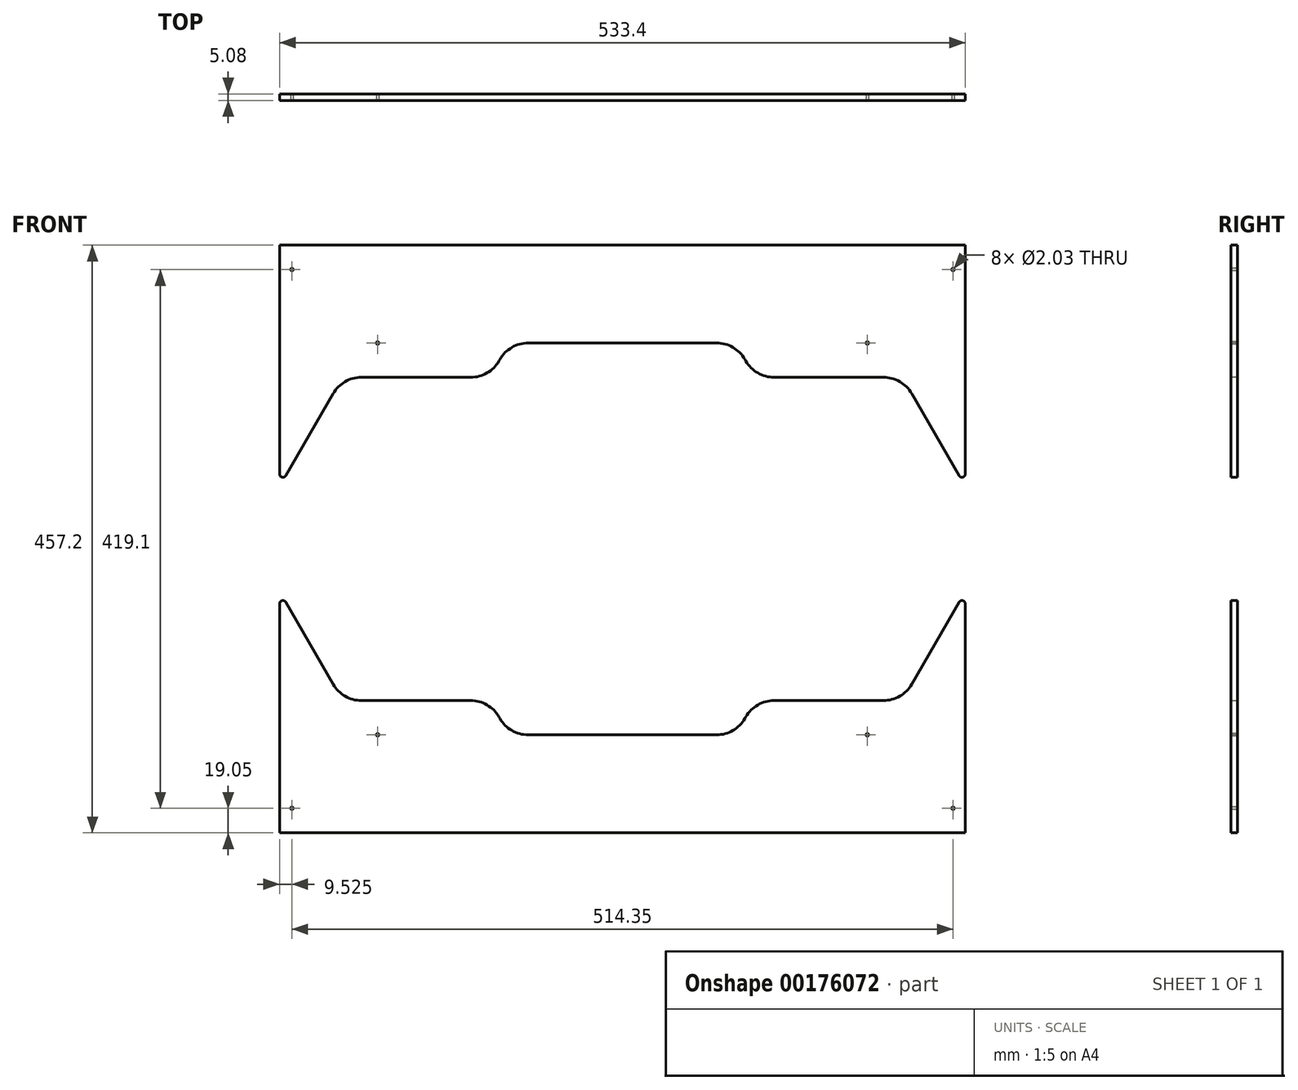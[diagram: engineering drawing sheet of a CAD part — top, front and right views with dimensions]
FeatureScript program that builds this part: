
annotation { "Feature Type Name" : "Feature", "Feature Type Description" : "" }
export const myFeature = defineFeature(function(context is Context, id is Id, definition is map)
    precondition{}
    {
        {
            var Q0;
            Q0=qCreatedBy(makeId("Front.planeOp"),FACE);
            var sketch = newSketch(context, id + "F0", { "sketchPlane" : qUnion([Q0])});
            skLineSegment(sketch, "E0.bottom", {"start": v(0, 0) * mm, "end": v(533.4, 0) * mm});
            skLineSegment(sketch, "E0.top", {"start": v(0, 457.2) * mm, "end": v(533.4, 457.2) * mm});
            skLineSegment(sketch, "E0.left", {"start": v(0, 0) * mm, "end": v(0, 457.2) * mm});
            skLineSegment(sketch, "E0.right", {"start": v(533.4, 0) * mm, "end": v(533.4, 457.2) * mm});
            skCircle(sketch, "E1.cCircle", {"center": v(121.52, 228.6) * mm, "radius": 125.73 * mm, "construction": true});
            skLineSegment(sketch, "E1.0", {"start": v(194.1, 354.33) * mm, "end": v(266.7, 228.6) * mm, "construction": true});
            skLineSegment(sketch, "E1.1", {"start": v(266.7, 228.6) * mm, "end": v(194.1, 102.87) * mm, "construction": true});
            skLineSegment(sketch, "E1.2", {"start": v(194.1, 102.87) * mm, "end": v(63.6, 102.87) * mm});
            skLineSegment(sketch, "E1.3", {"start": v(41.6, 115.57) * mm, "end": v(-16.33, 215.9) * mm});
            skLineSegment(sketch, "E1.4", {"start": v(-16.33, 241.3) * mm, "end": v(41.6, 341.63) * mm});
            skLineSegment(sketch, "E1.5", {"start": v(63.6, 354.33) * mm, "end": v(194.1, 354.33) * mm});
            skPoint(sketch, "E1.0.midPoint", {"position": v(230.4, 291.46) * mm});
            skCircle(sketch, "E2.cCircle", {"center": v(411.88, 228.6) * mm, "radius": 125.73 * mm, "construction": true});
            skLineSegment(sketch, "E2.0", {"start": v(491.8, 341.63) * mm, "end": v(549.73, 241.3) * mm});
            skLineSegment(sketch, "E2.1", {"start": v(549.73, 215.9) * mm, "end": v(491.8, 115.57) * mm});
            skLineSegment(sketch, "E2.2", {"start": v(469.8, 102.87) * mm, "end": v(339.3, 102.87) * mm});
            skLineSegment(sketch, "E2.3", {"start": v(339.3, 102.87) * mm, "end": v(266.7, 228.6) * mm, "construction": true});
            skLineSegment(sketch, "E2.4", {"start": v(266.7, 228.6) * mm, "end": v(339.3, 354.33) * mm, "construction": true});
            skLineSegment(sketch, "E2.5", {"start": v(339.3, 354.33) * mm, "end": v(469.8, 354.33) * mm});
            skPoint(sketch, "E2.0.midPoint", {"position": v(520.77, 291.46) * mm});
            skLineSegment(sketch, "E3", {"start": v(194.1, 354.33) * mm, "end": v(339.3, 354.33) * mm});
            skLineSegment(sketch, "E4", {"start": v(339.3, 102.87) * mm, "end": v(194.1, 102.87) * mm, "construction": true});
            skPoint(sketch, "E5.visualSharp", {"position": v(48.93, 354.33) * mm});
            skArc(sketch, "E5.filletArc", {"start": v(63.6, 354.33) * mm, "mid": v(50.9, 350.93) * mm, "end": v(41.6, 341.63) * mm});
            skPoint(sketch, "E6.visualSharp", {"position": v(-23.66, 228.6) * mm});
            skArc(sketch, "E6.filletArc", {"start": v(-16.33, 241.3) * mm, "mid": v(-19.73, 228.6) * mm, "end": v(-16.33, 215.9) * mm});
            skPoint(sketch, "E7.visualSharp", {"position": v(48.93, 102.87) * mm});
            skArc(sketch, "E7.filletArc", {"start": v(41.6, 115.57) * mm, "mid": v(50.9, 106.27) * mm, "end": v(63.6, 102.87) * mm});
            skPoint(sketch, "E8.visualSharp", {"position": v(484.47, 102.87) * mm});
            skArc(sketch, "E8.filletArc", {"start": v(469.8, 102.87) * mm, "mid": v(482.5, 106.27) * mm, "end": v(491.8, 115.57) * mm});
            skPoint(sketch, "E9.visualSharp", {"position": v(557.06, 228.6) * mm});
            skArc(sketch, "E9.filletArc", {"start": v(549.73, 215.9) * mm, "mid": v(553.13, 228.6) * mm, "end": v(549.73, 241.3) * mm});
            skPoint(sketch, "E10.visualSharp", {"position": v(484.47, 354.33) * mm});
            skArc(sketch, "E10.filletArc", {"start": v(491.8, 341.63) * mm, "mid": v(482.5, 350.93) * mm, "end": v(469.8, 354.33) * mm});
            skPoint(sketch, "E11", {"position": v(266.7, 457.2) * mm});
            skPoint(sketch, "E12", {"position": v(0, 228.6) * mm});
            skCircle(sketch, "E13.cCircle", {"center": v(266.7, 228.6) * mm, "radius": 125.73 * mm, "construction": true});
            skLineSegment(sketch, "E13.0", {"start": v(194.1, 354.33) * mm, "end": v(339.3, 354.33) * mm, "construction": true});
            skLineSegment(sketch, "E13.1", {"start": v(339.3, 354.33) * mm, "end": v(411.88, 228.6) * mm, "construction": true});
            skLineSegment(sketch, "E13.2", {"start": v(411.88, 228.6) * mm, "end": v(339.3, 102.87) * mm, "construction": true});
            skLineSegment(sketch, "E13.3", {"start": v(339.3, 102.87) * mm, "end": v(194.1, 102.87) * mm});
            skLineSegment(sketch, "E13.4", {"start": v(194.1, 102.87) * mm, "end": v(121.52, 228.6) * mm, "construction": true});
            skLineSegment(sketch, "E13.5", {"start": v(121.52, 228.6) * mm, "end": v(194.1, 354.33) * mm, "construction": true});
            skPoint(sketch, "E13.0.midPoint", {"position": v(266.7, 354.33) * mm});
            skLineSegment(sketch, "E14.bottom", {"start": v(196.06, 347.98) * mm, "end": v(221.46, 347.98) * mm});
            skLineSegment(sketch, "E14.top", {"start": v(196.06, 109.22) * mm, "end": v(221.46, 109.22) * mm});
            skLineSegment(sketch, "E14.left", {"start": v(196.06, 347.98) * mm, "end": v(196.06, 109.22) * mm});
            skLineSegment(sketch, "E14.right", {"start": v(221.46, 347.98) * mm, "end": v(221.46, 109.22) * mm});
            skLineSegment(sketch, "E15", {"start": v(208.76, 347.98) * mm, "end": v(208.76, 109.22) * mm, "construction": true});
            skPoint(sketch, "E16", {"position": v(208.76, 228.6) * mm});
            skLineSegment(sketch, "E17", {"start": v(266.7, 228.6) * mm, "end": v(266.7, 281.64) * mm, "construction": true});
            skLineSegment(sketch, "E18.MirrorCS", {"start": v(337.34, 109.22) * mm, "end": v(311.94, 109.22) * mm});
            skLineSegment(sketch, "E19.MirrorCS", {"start": v(311.94, 347.98) * mm, "end": v(311.94, 109.22) * mm});
            skLineSegment(sketch, "E20.MirrorCS", {"start": v(337.34, 347.98) * mm, "end": v(311.94, 347.98) * mm});
            skLineSegment(sketch, "E21.MirrorCS", {"start": v(337.34, 347.98) * mm, "end": v(337.34, 109.22) * mm});
            skSolve(sketch);
        }
        {
            var Q0;
            {var subQ1=sQuery(id+"F0.wireOp",EDGE,"E0.bottom");Q0=makeQuery(id+"F0.imprint","IMPRINT",FACE,{"disambiguationData":[TD([[makeQuery(id+"F0.imprint","IMPRINT",EDGE,{"derivedFrom":subQ1}),1.0]])]});}
            var Q1;
            {var subQ5=sQuery(id+"F0.wireOp",EDGE,"E0.top");Q1=makeQuery(id+"F0.imprint","IMPRINT",FACE,{"disambiguationData":[TD([[makeQuery(id+"F0.imprint","IMPRINT",EDGE,{"derivedFrom":subQ5}),-1.0]])]});}
            extrude(context, id + "F1", {"entities" : qUnion([Q0, Q1]), "depth" : 5.08 * mm});
        }
        {
            var Q0;
            Q0=makeQuery(id+"F1.opExtrude","CAP_FACE",FACE,{"disambiguationData":[OSD([sQuery(id+"F0.wireOp",EDGE,"E0.bottom"),sQuery(id+"F0.wireOp",EDGE,"E0.top"),sQuery(id+"F0.wireOp",EDGE,"E0.left"),sQuery(id+"F0.wireOp",EDGE,"E0.right"),sQuery(id+"F0.wireOp",EDGE,"E14.bottom"),sQuery(id+"F0.wireOp",EDGE,"E14.top"),sQuery(id+"F0.wireOp",EDGE,"E14.left"),sQuery(id+"F0.wireOp",EDGE,"E14.right"),sQuery(id+"F0.wireOp",EDGE,"E18.MirrorCS"),sQuery(id+"F0.wireOp",EDGE,"E19.MirrorCS"),sQuery(id+"F0.wireOp",EDGE,"E20.MirrorCS"),sQuery(id+"F0.wireOp",EDGE,"E21.MirrorCS")])],"isStart":false});
            var sketch = newSketch(context, id + "F2", { "sketchPlane" : qUnion([Q0])});
            skCircle(sketch, "E22", {"center": v(9.53, 438.15) * mm, "radius": 1.02 * mm});
            skCircle(sketch, "E23.0.1.0", {"center": v(9.53, 19.05) * mm, "radius": 1.02 * mm});
            skCircle(sketch, "E23.1.0.0", {"center": v(523.88, 438.15) * mm, "radius": 1.02 * mm});
            skCircle(sketch, "E23.1.1.0", {"center": v(523.88, 19.05) * mm, "radius": 1.02 * mm});
            skLineSegment(sketch, "E23.direction2", {"start": v(9.53, 438.15) * mm, "end": v(9.53, 19.05) * mm, "construction": true});
            skSolve(sketch);
        }
        {
            var Q0;
            Q0=makeQuery(id+"F2.imprint","IMPRINT",FACE,{"disambiguationData":[TD([[makeQuery(id+"F2.imprint","IMPRINT",EDGE,{"derivedFrom":sQuery(id+"F2.wireOp",EDGE,"E22")}),1.0]])]});
            var Q1;
            Q1=makeQuery(id+"F2.imprint","IMPRINT",FACE,{"disambiguationData":[TD([[makeQuery(id+"F2.imprint","IMPRINT",EDGE,{"derivedFrom":sQuery(id+"F2.wireOp",EDGE,"E23.1.0.0")}),1.0]])]});
            var Q2;
            Q2=makeQuery(id+"F2.imprint","IMPRINT",FACE,{"disambiguationData":[TD([[makeQuery(id+"F2.imprint","IMPRINT",EDGE,{"derivedFrom":sQuery(id+"F2.wireOp",EDGE,"E23.1.1.0")}),1.0]])]});
            var Q3;
            Q3=makeQuery(id+"F2.imprint","IMPRINT",FACE,{"disambiguationData":[TD([[makeQuery(id+"F2.imprint","IMPRINT",EDGE,{"derivedFrom":sQuery(id+"F2.wireOp",EDGE,"E23.0.1.0")}),1.0]])]});
            extrude(context, id + "F3", {"entities" : qUnion([Q0, Q1, Q2, Q3]), "operationType" : NewBodyOperationType.REMOVE, "endBound" : BoundingType.THROUGH_ALL, "oppositeDirection" : true, "depth" : 25.4 * mm});
        }
        {
            var Q0;
            Q0=makeQuery(id+"F1.opExtrude","CAP_FACE",FACE,{"disambiguationData":[OSD([sQuery(id+"F0.wireOp",EDGE,"E0.bottom"),sQuery(id+"F0.wireOp",EDGE,"E0.left"),sQuery(id+"F0.wireOp",EDGE,"E0.right"),sQuery(id+"F0.wireOp",EDGE,"E1.2"),sQuery(id+"F0.wireOp",EDGE,"E1.3"),sQuery(id+"F0.wireOp",EDGE,"E2.1"),sQuery(id+"F0.wireOp",EDGE,"E2.2"),sQuery(id+"F0.wireOp",EDGE,"E7.filletArc"),sQuery(id+"F0.wireOp",EDGE,"E8.filletArc"),sQuery(id+"F0.wireOp",EDGE,"E13.3")])],"isStart":false});
            var sketch = newSketch(context, id + "F4", { "sketchPlane" : qUnion([Q0])});
            skCircle(sketch, "E24", {"center": v(76.2, 381) * mm, "radius": 1.02 * mm});
            skCircle(sketch, "E25.0.1.0", {"center": v(76.2, 76.2) * mm, "radius": 1.02 * mm});
            skCircle(sketch, "E25.1.0.0", {"center": v(457.2, 381) * mm, "radius": 1.02 * mm});
            skCircle(sketch, "E25.1.1.0", {"center": v(457.2, 76.2) * mm, "radius": 1.02 * mm});
            skSolve(sketch);
        }
        {
            var Q0;
            Q0=makeQuery(id+"F4.imprint","IMPRINT",FACE,{"disambiguationData":[TD([[makeQuery(id+"F4.imprint","IMPRINT",EDGE,{"derivedFrom":sQuery(id+"F4.wireOp",EDGE,"E24")}),1.0]])]});
            var Q1;
            Q1=makeQuery(id+"F4.imprint","IMPRINT",FACE,{"disambiguationData":[TD([[makeQuery(id+"F4.imprint","IMPRINT",EDGE,{"derivedFrom":sQuery(id+"F4.wireOp",EDGE,"E25.1.1.0")}),1.0]])]});
            var Q2;
            Q2=makeQuery(id+"F4.imprint","IMPRINT",FACE,{"disambiguationData":[TD([[makeQuery(id+"F4.imprint","IMPRINT",EDGE,{"derivedFrom":sQuery(id+"F4.wireOp",EDGE,"E25.1.0.0")}),1.0]])]});
            var Q3;
            Q3=makeQuery(id+"F4.imprint","IMPRINT",FACE,{"disambiguationData":[TD([[makeQuery(id+"F4.imprint","IMPRINT",EDGE,{"derivedFrom":sQuery(id+"F4.wireOp",EDGE,"E25.0.1.0")}),1.0]])]});
            extrude(context, id + "F5", {"entities" : qUnion([Q0, Q1, Q2, Q3]), "operationType" : NewBodyOperationType.REMOVE, "endBound" : BoundingType.THROUGH_ALL, "oppositeDirection" : true, "depth" : 25.4 * mm});
        }
        {
            var Q0;
            Q0=makeQuery(id+"F1.opExtrude","CAP_FACE",FACE,{"disambiguationData":[OSD([sQuery(id+"F0.wireOp",EDGE,"E0.top"),sQuery(id+"F0.wireOp",EDGE,"E0.left"),sQuery(id+"F0.wireOp",EDGE,"E0.right"),sQuery(id+"F0.wireOp",EDGE,"E1.4"),sQuery(id+"F0.wireOp",EDGE,"E1.5"),sQuery(id+"F0.wireOp",EDGE,"E2.0"),sQuery(id+"F0.wireOp",EDGE,"E2.5"),sQuery(id+"F0.wireOp",EDGE,"E3"),sQuery(id+"F0.wireOp",EDGE,"E5.filletArc"),sQuery(id+"F0.wireOp",EDGE,"E10.filletArc")])],"isStart":false});
            var sketch = newSketch(context, id + "F6", { "sketchPlane" : qUnion([Q0])});
            skCircle(sketch, "E26.cCircle", {"center": v(266.7, 228.6) * mm, "radius": 127 * mm, "construction": true});
            skLineSegment(sketch, "E26.0", {"start": v(340.02, 355.6) * mm, "end": v(413.35, 228.6) * mm});
            skLineSegment(sketch, "E26.1", {"start": v(413.35, 228.6) * mm, "end": v(340.02, 101.6) * mm});
            skLineSegment(sketch, "E26.2", {"start": v(340.02, 101.6) * mm, "end": v(193.38, 101.6) * mm});
            skLineSegment(sketch, "E26.3", {"start": v(193.38, 101.6) * mm, "end": v(120.05, 228.6) * mm});
            skLineSegment(sketch, "E26.4", {"start": v(120.05, 228.6) * mm, "end": v(193.38, 355.6) * mm});
            skLineSegment(sketch, "E26.5", {"start": v(193.38, 355.6) * mm, "end": v(340.02, 355.6) * mm});
            skPoint(sketch, "E26.0.midPoint", {"position": v(376.69, 292.1) * mm});
            skCircle(sketch, "E27.cCircle", {"center": v(266.7, 228.6) * mm, "radius": 152.4 * mm, "construction": true});
            skLineSegment(sketch, "E27.0", {"start": v(193.38, 381) * mm, "end": v(340.02, 381) * mm});
            skLineSegment(sketch, "E27.1", {"start": v(362.02, 368.3) * mm, "end": v(442.68, 228.6) * mm});
            skLineSegment(sketch, "E27.2", {"start": v(442.68, 228.6) * mm, "end": v(362.02, 88.9) * mm});
            skLineSegment(sketch, "E27.3", {"start": v(340.02, 76.2) * mm, "end": v(193.38, 76.2) * mm});
            skLineSegment(sketch, "E27.4", {"start": v(171.38, 88.9) * mm, "end": v(90.72, 228.6) * mm});
            skLineSegment(sketch, "E27.5", {"start": v(90.72, 228.6) * mm, "end": v(171.38, 368.3) * mm});
            skPoint(sketch, "E27.0.midPoint", {"position": v(266.7, 381) * mm});
            skPoint(sketch, "E28.visualSharp", {"position": v(178.71, 381) * mm});
            skArc(sketch, "E28.filletArc", {"start": v(193.38, 381) * mm, "mid": v(180.68, 377.6) * mm, "end": v(171.38, 368.3) * mm});
            skPoint(sketch, "E29.visualSharp", {"position": v(354.69, 381) * mm});
            skArc(sketch, "E29.filletArc", {"start": v(362.02, 368.3) * mm, "mid": v(352.72, 377.6) * mm, "end": v(340.02, 381) * mm});
            skPoint(sketch, "E30.visualSharp", {"position": v(354.69, 76.2) * mm});
            skArc(sketch, "E30.filletArc", {"start": v(340.02, 76.2) * mm, "mid": v(352.72, 79.6) * mm, "end": v(362.02, 88.9) * mm});
            skPoint(sketch, "E31.visualSharp", {"position": v(178.71, 76.2) * mm});
            skArc(sketch, "E31.filletArc", {"start": v(171.38, 88.9) * mm, "mid": v(180.68, 79.6) * mm, "end": v(193.38, 76.2) * mm});
            skSolve(sketch);
        }
        {
            var Q0;
            {var subQ1=sQuery(id+"F6.wireOp",EDGE,"E26.1");Q0=makeQuery(id+"F6.imprint","IMPRINT",FACE,{"disambiguationData":[TD([[makeQuery(id+"F6.imprint","IMPRINT",EDGE,{"derivedFrom":subQ1}),-1.0]])]});}
            var Q1;
            {var subQ0=sQuery(id+"F6.wireOp",EDGE,"E26.5");Q1=makeQuery(id+"F6.imprint","IMPRINT",FACE,{"disambiguationData":[TD([[makeQuery(id+"F6.imprint","IMPRINT",EDGE,{"derivedFrom":subQ0}),-1.0]])]});}
            var Q2;
            {var subQ0=sQuery(id+"F6.wireOp",EDGE,"E26.5");Q2=makeQuery(id+"F6.imprint","IMPRINT",FACE,{"disambiguationData":[TD([[makeQuery(id+"F6.imprint","IMPRINT",EDGE,{"derivedFrom":subQ0}),1.0]])]});}
            var Q3;
            {var subQ12=sQuery(id+"F6.wireOp",EDGE,"E26.1");Q3=makeQuery(id+"F6.imprint","IMPRINT",FACE,{"disambiguationData":[TD([[makeQuery(id+"F6.imprint","IMPRINT",EDGE,{"derivedFrom":subQ12}),1.0]])]});}
            extrude(context, id + "F7", {"entities" : qUnion([Q0, Q1, Q2, Q3]), "operationType" : NewBodyOperationType.REMOVE, "endBound" : BoundingType.THROUGH_ALL, "oppositeDirection" : true, "depth" : 25.4 * mm});
        }
        {
            var Q0;
            Q0=makeQuery(id+"F7.boolean.opBoolean","INTERSECT",EDGE,{"derivedFrom":[makeQuery(id+"F1.opExtrude","SWEPT_FACE",FACE,{"disambiguationData":[OSD([sQuery(id+"F0.wireOp",EDGE,"E1.5"),sQuery(id+"F0.wireOp",EDGE,"E2.5"),sQuery(id+"F0.wireOp",EDGE,"E3")])]}),makeQuery(id+"F7.opExtrude","SWEPT_FACE",FACE,{"disambiguationData":[OSD([sQuery(id+"F6.wireOp",EDGE,"E27.5")])]})]});
            var Q1;
            Q1=makeQuery(id+"F7.boolean.opBoolean","INTERSECT",EDGE,{"derivedFrom":[makeQuery(id+"F1.opExtrude","SWEPT_FACE",FACE,{"disambiguationData":[OSD([sQuery(id+"F0.wireOp",EDGE,"E1.5"),sQuery(id+"F0.wireOp",EDGE,"E2.5"),sQuery(id+"F0.wireOp",EDGE,"E3")])]}),makeQuery(id+"F7.opExtrude","SWEPT_FACE",FACE,{"disambiguationData":[OSD([sQuery(id+"F6.wireOp",EDGE,"E27.1")])]})]});
            var Q2;
            Q2=makeQuery(id+"F7.boolean.opBoolean","INTERSECT",EDGE,{"derivedFrom":[makeQuery(id+"F1.opExtrude","SWEPT_FACE",FACE,{"disambiguationData":[OSD([sQuery(id+"F0.wireOp",EDGE,"E1.2"),sQuery(id+"F0.wireOp",EDGE,"E2.2"),sQuery(id+"F0.wireOp",EDGE,"E13.3")])]}),makeQuery(id+"F7.opExtrude","SWEPT_FACE",FACE,{"disambiguationData":[OSD([sQuery(id+"F6.wireOp",EDGE,"E27.4")])]})]});
            var Q3;
            Q3=makeQuery(id+"F7.boolean.opBoolean","INTERSECT",EDGE,{"derivedFrom":[makeQuery(id+"F1.opExtrude","SWEPT_FACE",FACE,{"disambiguationData":[OSD([sQuery(id+"F0.wireOp",EDGE,"E1.2"),sQuery(id+"F0.wireOp",EDGE,"E2.2"),sQuery(id+"F0.wireOp",EDGE,"E13.3")])]}),makeQuery(id+"F7.opExtrude","SWEPT_FACE",FACE,{"disambiguationData":[OSD([sQuery(id+"F6.wireOp",EDGE,"E27.2")])]})]});
            fillet(context, id + "F8", {"entities" : qUnion([Q0, Q1, Q2, Q3]), "radius" : 25.4 * mm, "tangentPropagation" : true, "allowEdgeOverflow" : false});
        }
        {
            var Q0;
            Q0=makeQuery(id+"F1.opExtrude","SWEPT_EDGE",EDGE,{"disambiguationData":[OSD([sQuery(id+"F0.wireOp",EDGE,"E0.left"),sQuery(id+"F0.wireOp",EDGE,"E1.4")])]});
            var Q1;
            Q1=makeQuery(id+"F1.opExtrude","SWEPT_EDGE",EDGE,{"disambiguationData":[OSD([sQuery(id+"F0.wireOp",EDGE,"E0.left"),sQuery(id+"F0.wireOp",EDGE,"E1.3")])]});
            var Q2;
            Q2=makeQuery(id+"F1.opExtrude","SWEPT_EDGE",EDGE,{"disambiguationData":[OSD([sQuery(id+"F0.wireOp",EDGE,"E0.right"),sQuery(id+"F0.wireOp",EDGE,"E2.0")])]});
            var Q3;
            Q3=makeQuery(id+"F1.opExtrude","SWEPT_EDGE",EDGE,{"disambiguationData":[OSD([sQuery(id+"F0.wireOp",EDGE,"E0.right"),sQuery(id+"F0.wireOp",EDGE,"E2.1")])]});
            fillet(context, id + "F9", {"entities" : qUnion([Q0, Q1, Q2, Q3]), "radius" : 2.54 * mm, "tangentPropagation" : true, "allowEdgeOverflow" : false});
        }
    });
